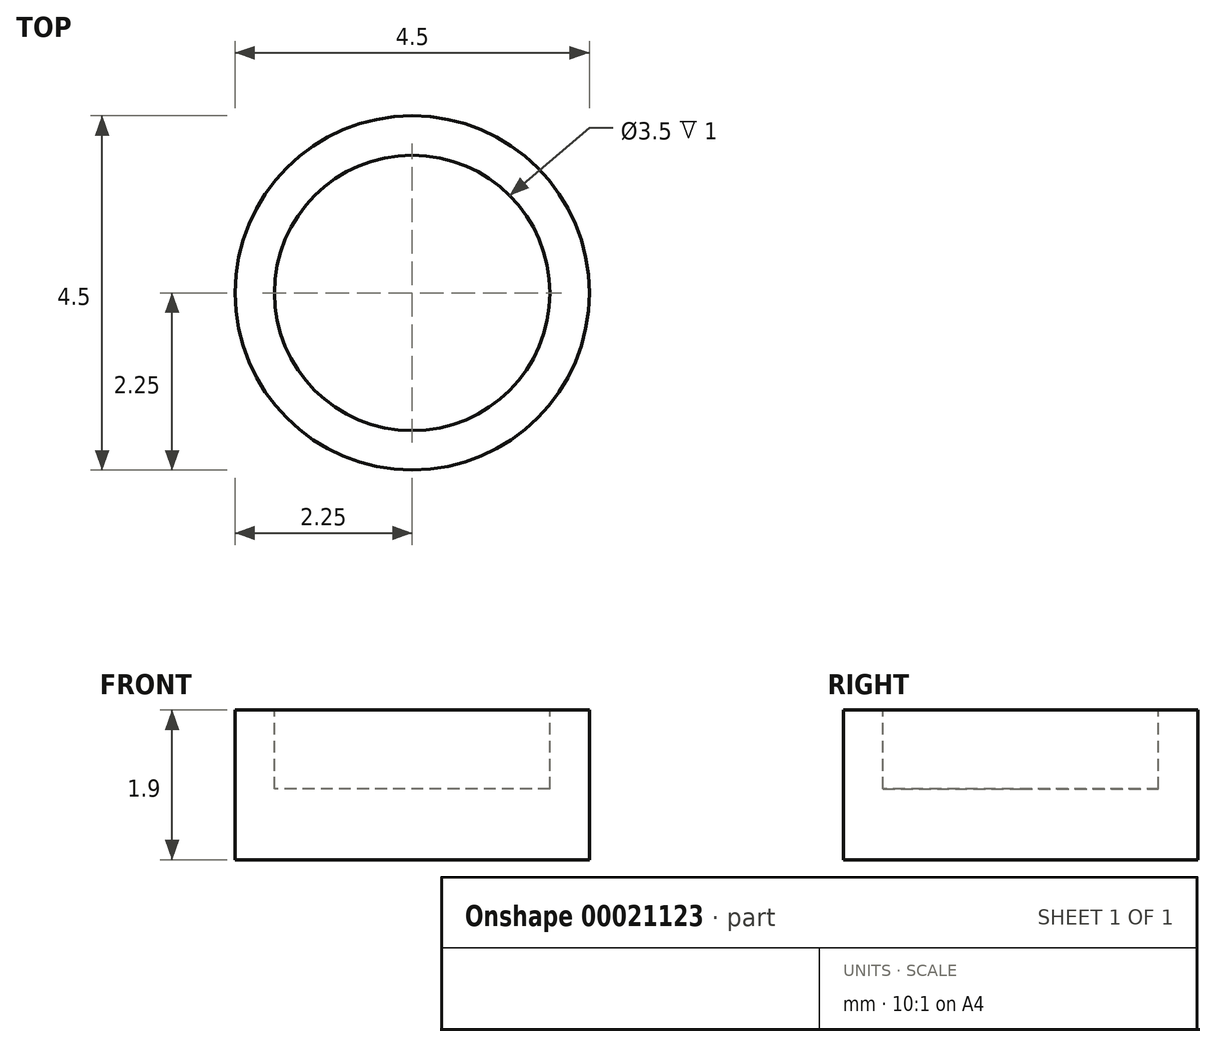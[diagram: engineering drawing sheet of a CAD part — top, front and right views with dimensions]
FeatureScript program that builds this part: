
annotation { "Feature Type Name" : "Feature", "Feature Type Description" : "" }
export const myFeature = defineFeature(function(context is Context, id is Id, definition is map)
    precondition{}
    {
        {
            var Q0;
            Q0=qCreatedBy(makeId("Top.planeOp"),FACE);
            var sketch = newSketch(context, id + "F0", { "sketchPlane" : qUnion([Q0])});
            skCircle(sketch, "E0", {"center": v(0, 0) * mm, "radius": 2.25 * mm});
            skSolve(sketch);
        }
        {
            var Q0;
            Q0 = qSketchRegion(id + "F0", true);
            extrude(context, id + "F1", {"entities" : qUnion([Q0]), "depth" : 1.9 * mm});
        }
        {
            var Q0;
            Q0=makeQuery(id+"F1.opExtrude","CAP_FACE",FACE,{"disambiguationData":[OSD([sQuery(id+"F0.wireOp",EDGE,"E0")])],"isStart":false});
            var sketch = newSketch(context, id + "F2", { "sketchPlane" : qUnion([Q0])});
            skCircle(sketch, "E1", {"center": v(0, 0) * mm, "radius": 1.75 * mm});
            skSolve(sketch);
        }
        {
            var Q0;
            Q0=makeQuery(id+"F2.imprint","IMPRINT",FACE,{"disambiguationData":[TD([[makeQuery(id+"F2.imprint","IMPRINT",EDGE,{"derivedFrom":sQuery(id+"F2.wireOp",EDGE,"E1")}),1.0]])]});
            extrude(context, id + "F3", {"entities" : qUnion([Q0]), "operationType" : NewBodyOperationType.REMOVE, "oppositeDirection" : true, "depth" : 1 * mm});
        }
    });
